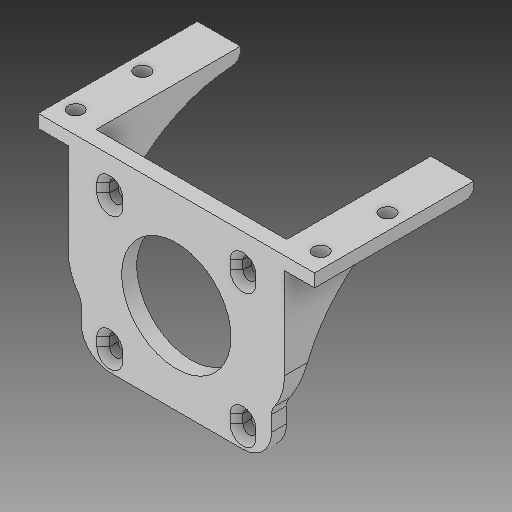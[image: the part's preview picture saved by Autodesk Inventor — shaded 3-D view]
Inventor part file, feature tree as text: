
AUTODESK INVENTOR PART (.ipt)
format: ipt  version: 2017 (Build 210142000, 142)  size: 294,400 bytes
history: native  units: in
note: dims shown in document units (in); Inventor stores cm internally (conversion verified against a paired STEP export)
features: extrude x7, sketch x7, reference x7, other x5, fillet x4, projected_geometry x2, chamfer x1
ambient origin geometry x8: Origin, YZ Plane, XZ Plane, XY Plane, X Axis, Y Axis, Z Axis, Center Point
bodies: Solid1 (feature_tree)
feature tree (33):
  extrude  "Extrusion1"  Depth=0.1378in
  extrude  "Extrusion3"  Depth=0.1181in TaperAngle=0.0deg
  extrude  "Extrusion4"  Depth=0.1181in TaperAngle=0.0deg
  extrude  "Extrusion5"  Depth=0.5in
  fillet  "Fillet1"  Radius=0.1181in
  fillet  "Fillet2"  Radius=0.1181in
  extrude  "Extrusion6"  Depth=0.1378in
  extrude  "Extrusion7"  Depth=0.0787in TaperAngle=0.0deg
  fillet  "Fillet3"  Radius=0.0787in
  fillet  "Fillet4"  Radius=0.0787in
  extrude  "Extrusion8"  Depth=0.0787in
  chamfer  "Chamfer1"  Distance=1.0in
  sketch  "Sketch1"  dims[d0=0.1378in d1=0.0in d4=0.0394in]
  reference  "Reference1"
  sketch  "Sketch3"  dims[d5=0.1181in d6=0.0in d7=0.1181in d8=0.0in]
  reference  "Reference2"
  sketch  "Sketch4"  dims[d9=0.1181in d10=0.2756in d11=0.0in]
  projected_geometry  "Projected Loop1"
  reference  "Reference3"
  sketch  "Sketch5"  dims[d12=0.125in d13=0.5in d14=0.1181in d15=0.1181in]
  sketch  "Sketch6"  dims[d16=0.2756in d17=0.0in d18=0.1378in]
  sketch  "Sketch7"  dims[d19=0.1378in d20=0.2756in d21=0.0in d22=0.0787in d23=0.0787in]
  reference  "Reference4"
  reference  "Reference5"
  sketch  "Sketch8"  dims[d24=1.0in d25=0.0787in d26=1.0in d27=0.0in d28=0.0591in d29=0.125in d30=45.0deg]
  projected_geometry  "Projected Loop2"
  reference  "Reference6"
  reference  "Reference7"
  other  "Rubiks Arm Assembly.iam"
  other  "Nema 17:1"
  other  "Base Plate:1"
  other  "Rubiks Cube Solver.iam"
  other  "bearing block:2"
